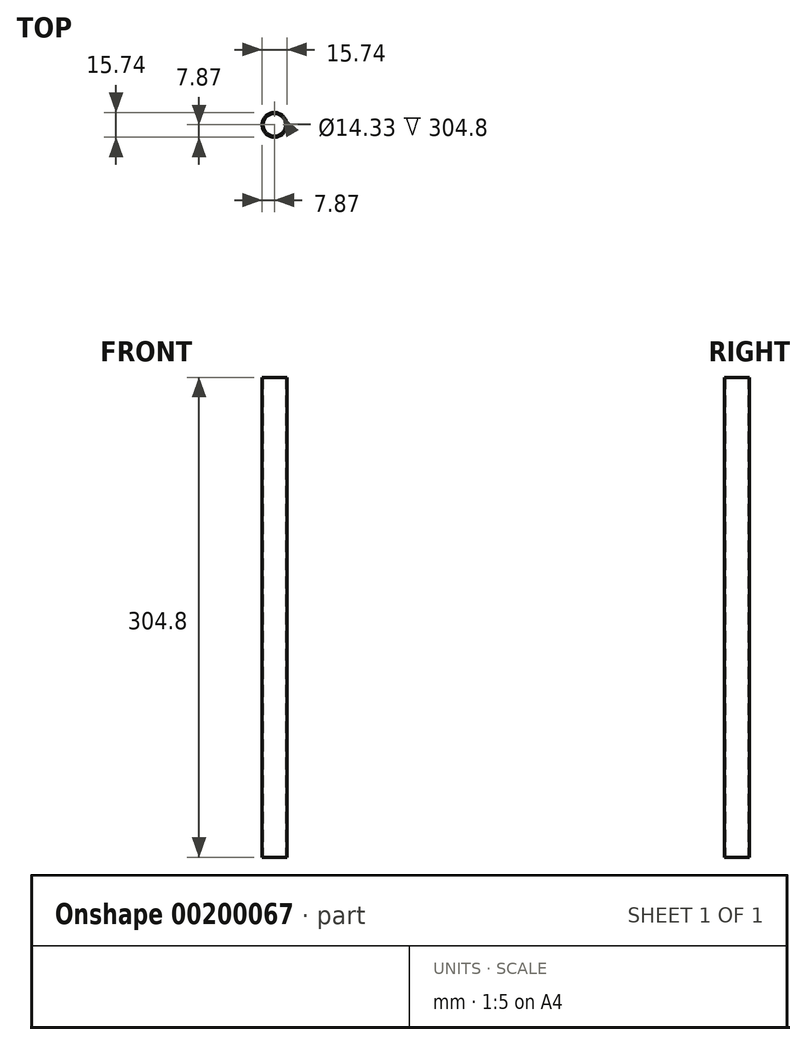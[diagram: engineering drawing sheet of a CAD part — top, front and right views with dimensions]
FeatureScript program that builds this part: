
annotation { "Feature Type Name" : "Feature", "Feature Type Description" : "" }
export const myFeature = defineFeature(function(context is Context, id is Id, definition is map)
    precondition{}
    {
        {
            var Q0;
            Q0=qCreatedBy(makeId("Top.planeOp"),FACE);
            var sketch = newSketch(context, id + "F0", { "sketchPlane" : qUnion([Q0])});
            skCircle(sketch, "E0", {"center": v(0, 0) * mm, "radius": 7.87 * mm});
            skCircle(sketch, "E1.0", {"center": v(0, 0) * mm, "radius": 7.16 * mm});
            skSolve(sketch);
        }
        {
            var Q0;
            Q0=makeQuery(id+"F0.imprint","IMPRINT",FACE,{"disambiguationData":[TD([[makeQuery(id+"F0.imprint","IMPRINT",EDGE,{"derivedFrom":sQuery(id+"F0.wireOp",EDGE,"E0")}),1.0]])]});
            extrude(context, id + "F1", {"entities" : qUnion([Q0]), "depth" : 304.8 * mm});
        }
    });
